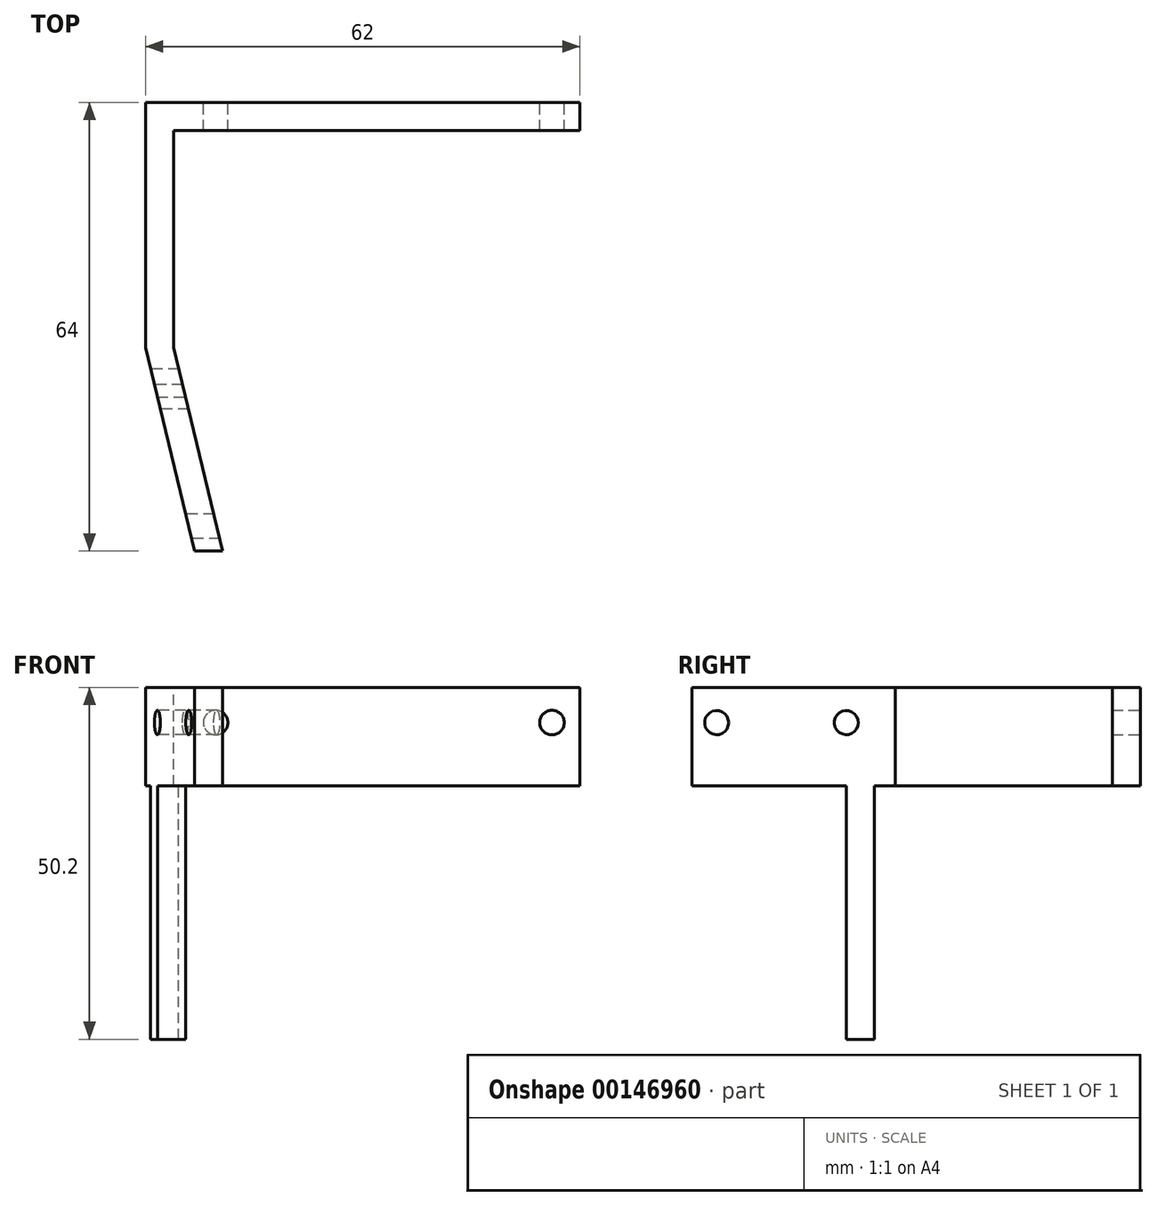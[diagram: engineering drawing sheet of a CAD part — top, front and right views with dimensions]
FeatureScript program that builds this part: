
annotation { "Feature Type Name" : "Feature", "Feature Type Description" : "" }
export const myFeature = defineFeature(function(context is Context, id is Id, definition is map)
    precondition{}
    {
        {
            var Q0;
            Q0=qCreatedBy(makeId("Front.planeOp"),FACE);
            var sketch = newSketch(context, id + "F0", { "sketchPlane" : qUnion([Q0])});
            skLineSegment(sketch, "E0", {"start": v(0, 0) * mm, "end": v(48, 0) * mm, "construction": true});
            skCircle(sketch, "E1", {"center": v(0, 0) * mm, "radius": 1.75 * mm});
            skCircle(sketch, "E2", {"center": v(48, 0) * mm, "radius": 1.75 * mm});
            skLineSegment(sketch, "E3", {"start": v(0, 0) * mm, "end": v(-6, 0) * mm, "construction": true});
            skLineSegment(sketch, "E4", {"start": v(48, 0) * mm, "end": v(52, 0) * mm, "construction": true});
            skLineSegment(sketch, "E5", {"start": v(-6, 0) * mm, "end": v(-6, 5) * mm});
            skLineSegment(sketch, "E6", {"start": v(-6, 5) * mm, "end": v(52, 5) * mm});
            skLineSegment(sketch, "E7", {"start": v(52, 5) * mm, "end": v(52, 0) * mm});
            skLineSegment(sketch, "E8", {"start": v(52, -9) * mm, "end": v(-6, -9) * mm});
            skLineSegment(sketch, "E9", {"start": v(-6, -9) * mm, "end": v(-6, 0) * mm});
            skLineSegment(sketch, "E10", {"start": v(52, -9) * mm, "end": v(52, 0) * mm});
            skSolve(sketch);
        }
        {
            var Q0;
            Q0=makeQuery(id+"F0.imprint","IMPRINT",FACE,{"disambiguationData":[TD([[makeQuery(id+"F0.imprint","IMPRINT",EDGE,{"derivedFrom":sQuery(id+"F0.wireOp",EDGE,"E1")}),-1.0]])]});
            extrude(context, id + "F1", {"entities" : qUnion([Q0]), "depth" : 4 * mm});
        }
        {
            var Q0;
            Q0=makeQuery(id+"F1.opExtrude","SWEPT_FACE",FACE,{"disambiguationData":[OSD([sQuery(id+"F0.wireOp",EDGE,"E5"),sQuery(id+"F0.wireOp",EDGE,"E9")])]});
            var sketch = newSketch(context, id + "F2", { "sketchPlane" : qUnion([Q0])});
            skLineSegment(sketch, "E11", {"start": v(0, 5) * mm, "end": v(64, 5) * mm});
            skLineSegment(sketch, "E12", {"start": v(64, 5) * mm, "end": v(64, -9) * mm});
            skPoint(sketch, "E12.endSnap0", {"position": v(2, -9) * mm});
            skLineSegment(sketch, "E13", {"start": v(64, -9) * mm, "end": v(0, -9) * mm});
            skLineSegment(sketch, "E14", {"start": v(0, -9) * mm, "end": v(0, 5) * mm});
            skLineSegment(sketch, "E15", {"start": v(4, 0) * mm, "end": v(42, 0) * mm, "construction": true});
            skCircle(sketch, "E16", {"center": v(42, 0) * mm, "radius": 1.6 * mm});
            skLineSegment(sketch, "E17", {"start": v(42, 0) * mm, "end": v(60, 0) * mm, "construction": true});
            skCircle(sketch, "E18", {"center": v(60, 0) * mm, "radius": 1.6 * mm});
            skSolve(sketch);
        }
        {
            var Q0;
            Q0=makeQuery(id+"F1.opExtrude","SWEPT_FACE",FACE,{"disambiguationData":[OSD([sQuery(id+"F0.wireOp",EDGE,"E6")])]});
            var sketch = newSketch(context, id + "F3", { "sketchPlane" : qUnion([Q0])});
            skLineSegment(sketch, "E19", {"start": v(-10, -35) * mm, "end": v(-6, -35) * mm});
            skLineSegment(sketch, "E20", {"start": v(-10, -64) * mm, "end": v(-3, -64) * mm, "construction": true});
            skLineSegment(sketch, "E21", {"start": v(-3, -64) * mm, "end": v(1, -64) * mm});
            skLineSegment(sketch, "E22", {"start": v(-3, -64) * mm, "end": v(-10, -35) * mm});
            skLineSegment(sketch, "E23", {"start": v(1, -64) * mm, "end": v(-6, -35) * mm});
            skLineSegment(sketch, "E24.bottom", {"start": v(-6, 0) * mm, "end": v(-10, 0) * mm});
            skLineSegment(sketch, "E24.top", {"start": v(-6, -64) * mm, "end": v(-10, -64) * mm});
            skLineSegment(sketch, "E24.left", {"start": v(-6, 0) * mm, "end": v(-6, -64) * mm});
            skLineSegment(sketch, "E24.right", {"start": v(-10, 0) * mm, "end": v(-10, -64) * mm});
            skLineSegment(sketch, "E25", {"start": v(-9.28, -38) * mm, "end": v(-5.28, -38) * mm});
            skLineSegment(sketch, "E26", {"start": v(-4.31, -42) * mm, "end": v(-8.31, -42) * mm});
            skSolve(sketch);
        }
        {
            var Q0;
            {var subQ3=sQuery(id+"F3.wireOp",EDGE,"E23");Q0=makeQuery(id+"F3.imprint","IMPRINT",FACE,{"disambiguationData":[TD([[makeQuery(id+"F3.imprint","IMPRINT",EDGE,{"derivedFrom":subQ3}),1.0]])]});}
            var Q1;
            {var subQ0=sQuery(id+"F3.wireOp",EDGE,"E19");Q1=makeQuery(id+"F3.imprint","IMPRINT",FACE,{"disambiguationData":[TD([[makeQuery(id+"F3.imprint","IMPRINT",EDGE,{"derivedFrom":subQ0}),-1.0]])]});}
            var Q2;
            {var subQ4=sQuery(id+"F3.wireOp",EDGE,"E19");Q2=makeQuery(id+"F3.imprint","IMPRINT",FACE,{"disambiguationData":[TD([[makeQuery(id+"F3.imprint","IMPRINT",EDGE,{"derivedFrom":subQ4}),1.0]])]});}
            var Q3;
            {var subQ0=sQuery(id+"F3.wireOp",EDGE,"E25");var subQ1=sQuery(id+"F3.wireOp",EDGE,"E22");var subQ2=makeQuery(id+"F3.imprint","INTERSECT",VERTEX,{"derivedFrom":[subQ1,subQ0]});Q3=makeQuery(id+"F3.imprint","IMPRINT",FACE,{"disambiguationData":[TD([[makeQuery(id+"F3.imprint","IMPRINT",EDGE,{"disambiguationData":[TD([[subQ2,1.0]])],"derivedFrom":subQ1}),-1.0]])]});}
            var Q4;
            {var subQ0=sQuery(id+"F3.wireOp",EDGE,"E24.top");var subQ1=sQuery(id+"F3.wireOp",EDGE,"E22");var subQ2=makeQuery(id+"F3.imprint","INTERSECT",VERTEX,{"derivedFrom":[subQ1,subQ0]});Q4=makeQuery(id+"F3.imprint","IMPRINT",FACE,{"disambiguationData":[TD([[makeQuery(id+"F3.imprint","IMPRINT",EDGE,{"disambiguationData":[TD([[subQ2,-1.0]])],"derivedFrom":subQ1}),-1.0]])]});}
            var Q5;
            {var subQ0=sQuery(id+"F3.wireOp",EDGE,"E21");Q5=makeQuery(id+"F3.imprint","IMPRINT",FACE,{"disambiguationData":[TD([[makeQuery(id+"F3.imprint","IMPRINT",EDGE,{"derivedFrom":subQ0}),1.0]])]});}
            var Q6;
            {var subQ0=sQuery(id+"F3.wireOp",EDGE,"E25");var subQ1=sQuery(id+"F3.wireOp",EDGE,"E23");var subQ2=makeQuery(id+"F3.imprint","INTERSECT",VERTEX,{"derivedFrom":[subQ1,subQ0]});Q6=makeQuery(id+"F3.imprint","IMPRINT",FACE,{"disambiguationData":[TD([[makeQuery(id+"F3.imprint","IMPRINT",EDGE,{"disambiguationData":[TD([[subQ2,1.0]])],"derivedFrom":subQ1}),1.0]])]});}
            extrude(context, id + "F4", {"entities" : qUnion([Q0, Q1, Q2, Q3, Q4, Q5, Q6]), "operationType" : NewBodyOperationType.ADD, "oppositeDirection" : true, "depth" : 14 * mm, "offsetDistance" : 25 * mm});
        }
        {
            var Q0;
            Q0=makeQuery(id+"F4.opExtrude","SWEPT_FACE",FACE,{"disambiguationData":[OSD([sQuery(id+"F3.wireOp",EDGE,"E24.right")])]});
            var sketch = newSketch(context, id + "F5", { "sketchPlane" : qUnion([Q0])});
            skLineSegment(sketch, "E27", {"start": v(0, -9) * mm, "end": v(0, 0) * mm, "construction": true});
            skLineSegment(sketch, "E28", {"start": v(0, 0) * mm, "end": v(42, 0) * mm, "construction": true});
            skLineSegment(sketch, "E29", {"start": v(42, 0) * mm, "end": v(60.5, 0) * mm, "construction": true});
            skCircle(sketch, "E30", {"center": v(42, 0) * mm, "radius": 1.75 * mm});
            skCircle(sketch, "E31", {"center": v(60.5, 0) * mm, "radius": 1.75 * mm});
            skSolve(sketch);
        }
        {
            var Q0;
            {var subQ0=sQuery(id+"F3.wireOp",EDGE,"E25");var subQ1=sQuery(id+"F3.wireOp",EDGE,"E22");var subQ2=makeQuery(id+"F3.imprint","INTERSECT",VERTEX,{"derivedFrom":[subQ1,subQ0]});Q0=makeQuery(id+"F3.imprint","IMPRINT",FACE,{"disambiguationData":[TD([[makeQuery(id+"F3.imprint","IMPRINT",EDGE,{"disambiguationData":[TD([[subQ2,1.0]])],"derivedFrom":subQ1}),-1.0]])]});}
            var Q1;
            {var subQ0=sQuery(id+"F3.wireOp",EDGE,"E25");var subQ1=sQuery(id+"F3.wireOp",EDGE,"E23");var subQ2=makeQuery(id+"F3.imprint","INTERSECT",VERTEX,{"derivedFrom":[subQ1,subQ0]});Q1=makeQuery(id+"F3.imprint","IMPRINT",FACE,{"disambiguationData":[TD([[makeQuery(id+"F3.imprint","IMPRINT",EDGE,{"disambiguationData":[TD([[subQ2,1.0]])],"derivedFrom":subQ1}),1.0]])]});}
            extrude(context, id + "F6", {"entities" : qUnion([Q0, Q1]), "operationType" : NewBodyOperationType.ADD, "oppositeDirection" : true, "depth" : 50.2 * mm, "offsetDistance" : 25 * mm});
        }
        {
            var Q0;
            Q0=makeQuery(id+"F5.imprint","IMPRINT",FACE,{"disambiguationData":[TD([[makeQuery(id+"F5.imprint","IMPRINT",EDGE,{"derivedFrom":sQuery(id+"F5.wireOp",EDGE,"E30")}),1.0]])]});
            var Q1;
            Q1=makeQuery(id+"F5.imprint","IMPRINT",FACE,{"disambiguationData":[TD([[makeQuery(id+"F5.imprint","IMPRINT",EDGE,{"derivedFrom":sQuery(id+"F5.wireOp",EDGE,"E31")}),1.0]])]});
            extrude(context, id + "F7", {"entities" : qUnion([Q0, Q1]), "operationType" : NewBodyOperationType.REMOVE, "oppositeDirection" : true, "depth" : 71 * mm, "offsetDistance" : 25 * mm});
        }
    });
